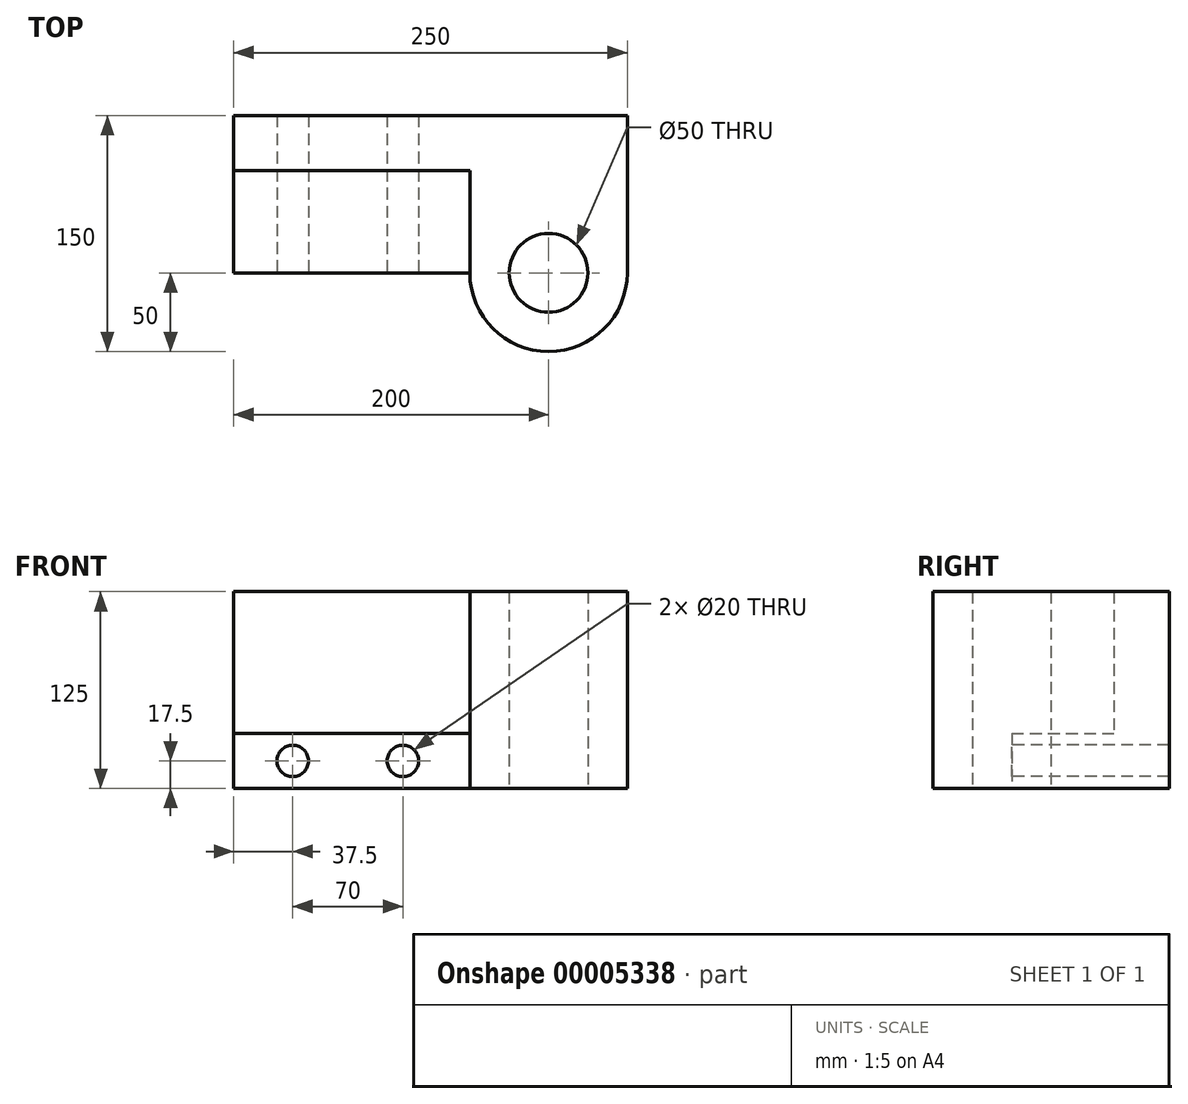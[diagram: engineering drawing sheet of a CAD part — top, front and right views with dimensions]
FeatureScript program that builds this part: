
annotation { "Feature Type Name" : "Feature", "Feature Type Description" : "" }
export const myFeature = defineFeature(function(context is Context, id is Id, definition is map)
    precondition{}
    {
        {
            var Q0;
            Q0=qCreatedBy(makeId("Top.planeOp"),FACE);
            var sketch = newSketch(context, id + "F0", { "sketchPlane" : qUnion([Q0])});
            skCircle(sketch, "E0", {"center": v(0, 0) * mm, "radius": 25 * mm});
            skArc(sketch, "E1", {"start": v(-50, 0) * mm, "mid": v(0, -50) * mm, "end": v(50, 0) * mm});
            skLineSegment(sketch, "E2", {"start": v(50, 0) * mm, "end": v(50, 100) * mm});
            skLineSegment(sketch, "E3", {"start": v(50, 100) * mm, "end": v(-200, 100) * mm});
            skLineSegment(sketch, "E4", {"start": v(-200, 100) * mm, "end": v(-200, 65) * mm});
            skLineSegment(sketch, "E5", {"start": v(-50, 0) * mm, "end": v(-50, 65) * mm});
            skLineSegment(sketch, "E6", {"start": v(-50, 65) * mm, "end": v(-200, 65) * mm});
            skSolve(sketch);
        }
        {
            var Q0;
            Q0 = qSketchRegion(id + "F0", true);
            extrude(context, id + "F1", {"entities" : qUnion([Q0]), "depth" : 125 * mm});
        }
        {
            var Q0;
            Q0=makeQuery(id+"F1.opExtrude","SWEPT_FACE",FACE,{"disambiguationData":[OSD([sQuery(id+"F0.wireOp",EDGE,"E6")])]});
            var sketch = newSketch(context, id + "F2", { "sketchPlane" : qUnion([Q0])});
            skLineSegment(sketch, "E7.bottom", {"start": v(-200, 0) * mm, "end": v(-50, 0) * mm});
            skLineSegment(sketch, "E7.top", {"start": v(-200, 35) * mm, "end": v(-50, 35) * mm});
            skLineSegment(sketch, "E7.left", {"start": v(-200, 0) * mm, "end": v(-200, 35) * mm});
            skLineSegment(sketch, "E7.right", {"start": v(-50, 0) * mm, "end": v(-50, 35) * mm});
            skSolve(sketch);
        }
        {
            var Q0;
            Q0 = qSketchRegion(id + "F2", true);
            extrude(context, id + "F3", {"entities" : qUnion([Q0]), "operationType" : NewBodyOperationType.ADD, "depth" : 65 * mm});
        }
        {
            var Q0;
            Q0=makeQuery(id+"F3.opExtrude","CAP_FACE",FACE,{"disambiguationData":[OSD([sQuery(id+"F2.wireOp",EDGE,"E7.bottom"),sQuery(id+"F2.wireOp",EDGE,"E7.top"),sQuery(id+"F2.wireOp",EDGE,"E7.left"),sQuery(id+"F2.wireOp",EDGE,"E7.right")])],"isStart":false});
            var sketch = newSketch(context, id + "F4", { "sketchPlane" : qUnion([Q0])});
            skCircle(sketch, "E8", {"center": v(-162.5, 17.5) * mm, "radius": 10 * mm});
            skCircle(sketch, "E9", {"center": v(-92.5, 17.5) * mm, "radius": 10 * mm});
            skSolve(sketch);
        }
        {
            var Q0;
            Q0 = qSketchRegion(id + "F4", true);
            extrude(context, id + "F5", {"entities" : qUnion([Q0]), "operationType" : NewBodyOperationType.REMOVE, "endBound" : BoundingType.THROUGH_ALL, "oppositeDirection" : true, "depth" : 25 * mm});
        }
    });
